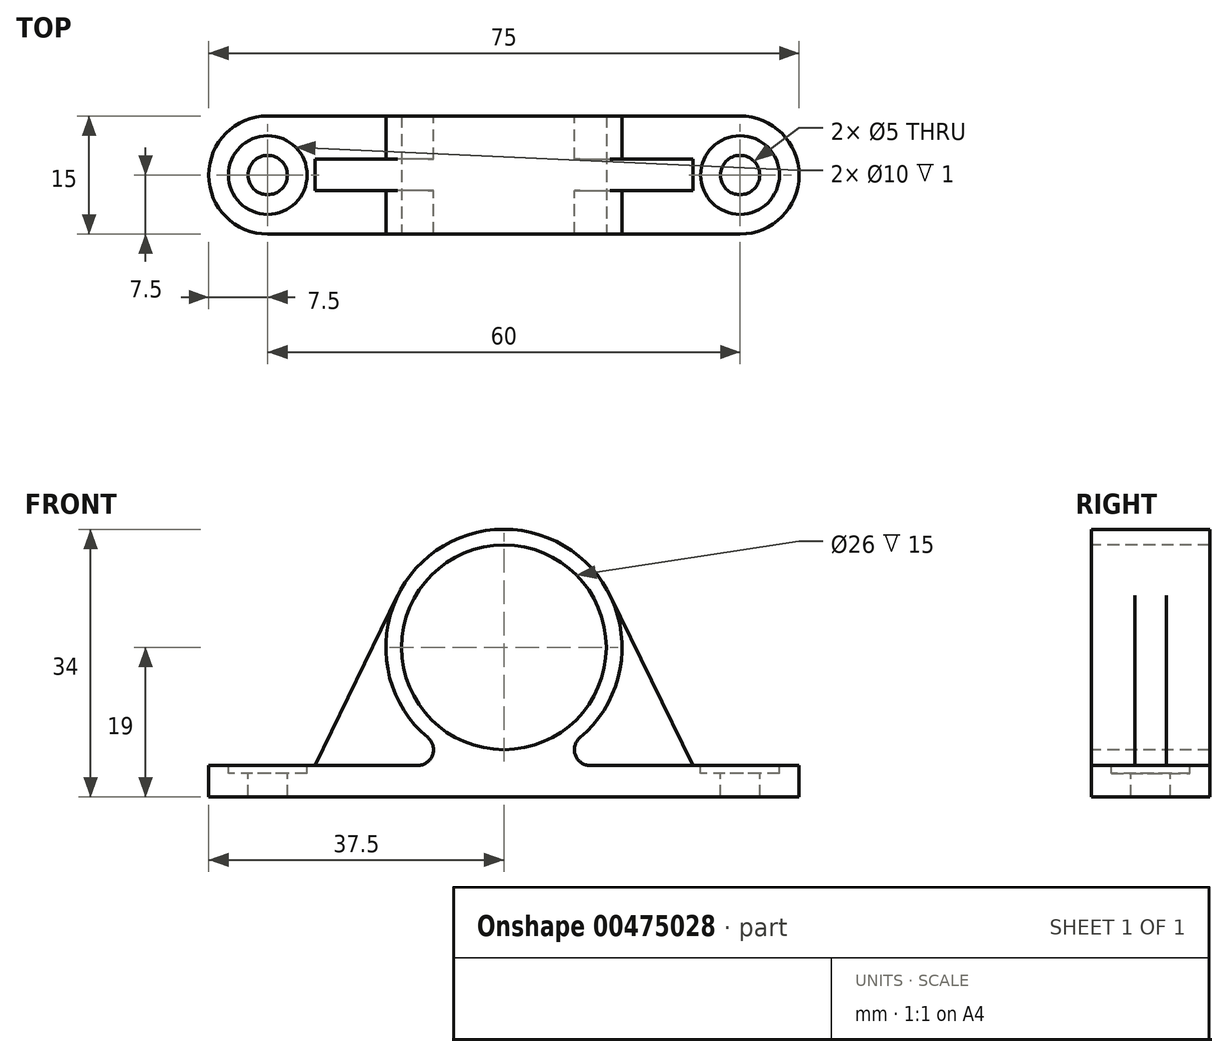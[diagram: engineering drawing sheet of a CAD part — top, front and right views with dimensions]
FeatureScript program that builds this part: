
annotation { "Feature Type Name" : "Feature", "Feature Type Description" : "" }
export const myFeature = defineFeature(function(context is Context, id is Id, definition is map)
    precondition{}
    {
        {
            assignVariable(context, id + "F0", {"name" : "Thickness", "anyValue" : 15});
        }
        {
            var Q0;
            Q0=qCreatedBy(makeId("Front.planeOp"),FACE);
            var sketch = newSketch(context, id + "F1", { "sketchPlane" : qUnion([Q0])});
            skLineSegment(sketch, "E0", {"start": v(0, 0) * mm, "end": v(-37.5, 0) * mm});
            skLineSegment(sketch, "E1", {"start": v(-37.5, 0) * mm, "end": v(-37.5, 4) * mm});
            skLineSegment(sketch, "E2", {"start": v(-37.5, 4) * mm, "end": v(-10.95, 4) * mm});
            skLineSegment(sketch, "E3", {"start": v(0, -14.72) * mm, "end": v(0, 62.74) * mm, "construction": true});
            skArc(sketch, "E4", {"start": v(-9.67, 7.53) * mm, "mid": v(-14.1, 24.14) * mm, "end": v(0, 34) * mm});
            skPoint(sketch, "E5.visualSharp", {"position": v(0, 4) * mm});
            skArc(sketch, "E5.filletArc", {"start": v(-10.95, 4) * mm, "mid": v(-9.08, 5.31) * mm, "end": v(-9.67, 7.53) * mm});
            skLineSegment(sketch, "E6.MirrorCS", {"start": v(37.5, 0) * mm, "end": v(37.5, 4) * mm});
            skLineSegment(sketch, "E7.MirrorCS", {"start": v(37.5, 4) * mm, "end": v(10.95, 4) * mm});
            skLineSegment(sketch, "E8.MirrorCS", {"start": v(0, 0) * mm, "end": v(37.5, 0) * mm});
            skArc(sketch, "E9.MirrorCS", {"start": v(9.67, 7.53) * mm, "mid": v(14.1, 24.14) * mm, "end": v(0, 34) * mm});
            skArc(sketch, "E10.MirrorCS", {"start": v(10.95, 4) * mm, "mid": v(9.08, 5.31) * mm, "end": v(9.67, 7.53) * mm});
            skArc(sketch, "E11", {"start": v(-9.67, 7.53) * mm, "mid": v(0, 4) * mm, "end": v(9.67, 7.53) * mm, "construction": true});
            skSolve(sketch);
        }
        {
            var Q0;
            Q0=qSketchRegion(id+"F1",true);
            extrude(context, id + "F2", {"entities" : qUnion([Q0]), "endBound" : BoundingType.SYMMETRIC, "depth" : 15 * mm});
        }
        {
            var Q0;
            Q0=makeQuery(id+"F2.opExtrude","CAP_FACE",FACE,{"disambiguationData":[OSD([sQuery(id+"F1.wireOp",EDGE,"E0"),sQuery(id+"F1.wireOp",EDGE,"E1"),sQuery(id+"F1.wireOp",EDGE,"E2"),sQuery(id+"F1.wireOp",EDGE,"E5.filletArc"),sQuery(id+"F1.wireOp",EDGE,"E6.MirrorCS"),sQuery(id+"F1.wireOp",EDGE,"E7.MirrorCS"),sQuery(id+"F1.wireOp",EDGE,"E8.MirrorCS"),sQuery(id+"F1.wireOp",EDGE,"E9.MirrorCS"),sQuery(id+"F1.wireOp",EDGE,"E10.MirrorCS"),sQuery(id+"F1.wireOp",EDGE,"E4")])],"isStart":false});
            var sketch = newSketch(context, id + "F3", { "sketchPlane" : qUnion([Q0])});
            skCircle(sketch, "E12", {"center": v(0, 19) * mm, "radius": 13 * mm});
            skSolve(sketch);
        }
        {
            var Q0;
            Q0=qSketchRegion(id+"F3",true);
            extrude(context, id + "F4", {"entities" : qUnion([Q0]), "operationType" : NewBodyOperationType.REMOVE, "endBound" : BoundingType.THROUGH_ALL, "oppositeDirection" : true, "depth" : (getVariable(context, 'Thickness') - 3) * mm});
        }
        {
            var Q0;
            Q0=makeQuery(id+"F2.opExtrude","CAP_EDGE",EDGE,{"disambiguationData":[OSD([sQuery(id+"F1.wireOp",EDGE,"E6.MirrorCS")])],"isStart":false});
            var Q1;
            Q1=makeQuery(id+"F2.opExtrude","CAP_EDGE",EDGE,{"disambiguationData":[OSD([sQuery(id+"F1.wireOp",EDGE,"E6.MirrorCS")])],"isStart":true});
            var Q2;
            Q2=makeQuery(id+"F2.opExtrude","CAP_EDGE",EDGE,{"disambiguationData":[OSD([sQuery(id+"F1.wireOp",EDGE,"E1")])],"isStart":false});
            var Q3;
            Q3=makeQuery(id+"F2.opExtrude","CAP_EDGE",EDGE,{"disambiguationData":[OSD([sQuery(id+"F1.wireOp",EDGE,"E1")])],"isStart":true});
            fillet(context, id + "F5", {"entities" : qUnion([Q0, Q1, Q2, Q3]), "radius" : (getVariable(context, 'Thickness') / 2) * mm, "tangentPropagation" : true, "allowEdgeOverflow" : false});
        }
        {
            var Q0;
            Q0=makeQuery(id+"F2.opExtrude","SWEPT_FACE",FACE,{"disambiguationData":[OSD([sQuery(id+"F1.wireOp",EDGE,"E7.MirrorCS")])]});
            var sketch = newSketch(context, id + "F6", { "sketchPlane" : qUnion([Q0])});
            skPoint(sketch, "E13", {"position": v(30, 0) * mm});
            skPoint(sketch, "E14.MirrorP", {"position": v(-30, 0) * mm});
            skSolve(sketch);
        }
        {
            var Q0;
            Q0=sQuery(id+"F6.wireOp",VERTEX,"E13");
            var Q1;
            Q1=sQuery(id+"F6.wireOp",VERTEX,"E14.MirrorP");
            var Q2;
            Q2=makeQuery(id+"F2.opExtrude","SWEPT_BODY",BODY,{"disambiguationData":[OSD([sQuery(id+"F1.wireOp",EDGE,"E0"),sQuery(id+"F1.wireOp",EDGE,"E1"),sQuery(id+"F1.wireOp",EDGE,"E2"),sQuery(id+"F1.wireOp",EDGE,"E5.filletArc"),sQuery(id+"F1.wireOp",EDGE,"E6.MirrorCS"),sQuery(id+"F1.wireOp",EDGE,"E7.MirrorCS"),sQuery(id+"F1.wireOp",EDGE,"E8.MirrorCS"),sQuery(id+"F1.wireOp",EDGE,"E9.MirrorCS"),sQuery(id+"F1.wireOp",EDGE,"E10.MirrorCS"),sQuery(id+"F1.wireOp",EDGE,"E4"),sQuery(id+"F1.wireOp",EDGE,"xOvTdpff-GPNy-Ahw4-pvuq-FGurvRJnDwLL"),sQuery(id+"F1.wireOp",EDGE,"c4084a71-2947-44b7-b196-35892ec3426b0.MirrorCS")])]});
            hole(context, id + "F7", {"style" : HoleStyle.C_BORE, "endStyle" : HoleEndStyle.THROUGH, "holeDiameter" : 5 * mm, "cBoreDiameter" : 10 * mm, "cBoreDepth" : 1 * mm, "isTappedThrough" : true, "tappedDepth" : 12 * mm, "tapClearance" : 3, "locations" : qUnion([Q0, Q1]), "scope" : qUnion([Q2])});
        }
        {
            var Q0;
            Q0=qCreatedBy(makeId("Front.planeOp"),FACE);
            var sketch = newSketch(context, id + "F8", { "sketchPlane" : qUnion([Q0])});
            skLineSegment(sketch, "E15", {"start": v(24, 4) * mm, "end": v(13.48, 25.57) * mm});
            skArc(sketch, "E16.0", {"start": v(9.67, 7.53) * mm, "mid": v(14.68, 15.9) * mm, "end": v(13.48, 25.57) * mm});
            skArc(sketch, "E17.0", {"start": v(10.95, 4) * mm, "mid": v(9.08, 5.31) * mm, "end": v(9.67, 7.53) * mm});
            skPoint(sketch, "E18.0", {"position": v(10.95, 4) * mm});
            skLineSegment(sketch, "E19", {"start": v(10.95, 4) * mm, "end": v(24, 4) * mm});
            skLineSegment(sketch, "E20.0", {"start": v(25, 4) * mm, "end": v(35, 4) * mm, "construction": true});
            skSolve(sketch);
        }
        {
            var Q0;
            {var subQ0=sQuery(id+"F8.wireOp",EDGE,"E15");Q0=makeQuery(id+"F8.imprint","IMPRINT",FACE,{"disambiguationData":[TD([[makeQuery(id+"F8.imprint","IMPRINT",EDGE,{"derivedFrom":subQ0}),1.0]])]});}
            extrude(context, id + "F9", {"entities" : qUnion([Q0]), "endBound" : BoundingType.SYMMETRIC, "depth" : 4 * mm});
        }
        {
            var Q0;
            Q0=makeQuery(id+"F9.opExtrude","SWEPT_BODY",BODY,{"disambiguationData":[OSD([sQuery(id+"F8.wireOp",EDGE,"E15"),sQuery(id+"F8.wireOp",EDGE,"E16.0"),sQuery(id+"F8.wireOp",EDGE,"E17.0"),sQuery(id+"F8.wireOp",EDGE,"d5b68f82-8350-41d3-9ff2-1b9ca3f2bff8.0")])]});
            var Q1;
            Q1=qCreatedBy(makeId("Right.planeOp"),FACE);
            mirror(context, id + "F10", {"operationType" : NewBodyOperationType.ADD, "entities" : qUnion([Q0]), "mirrorPlane" : qUnion([Q1])});
        }
    });
